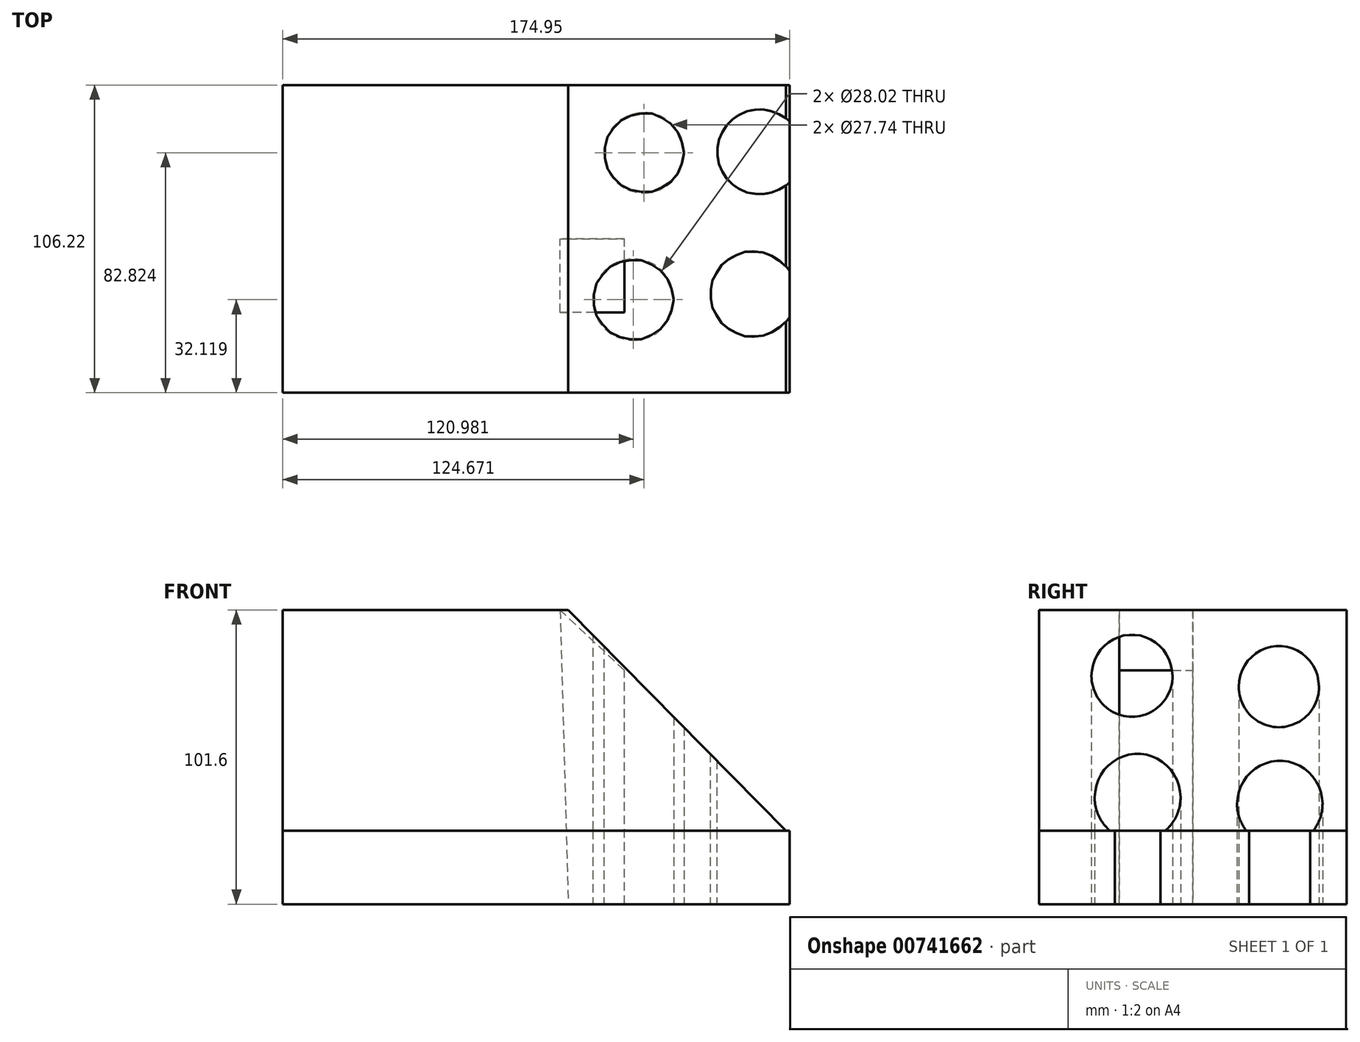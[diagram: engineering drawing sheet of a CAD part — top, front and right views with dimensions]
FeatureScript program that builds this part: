
annotation { "Feature Type Name" : "Feature", "Feature Type Description" : "" }
export const myFeature = defineFeature(function(context is Context, id is Id, definition is map)
    precondition{}
    {
        {
            var Q0;
            Q0=qCreatedBy(makeId("Top.planeOp"),FACE);
            var sketch = newSketch(context, id + "F0", { "sketchPlane" : qUnion([Q0])});
            skLineSegment(sketch, "E0.bottom", {"start": v(98.54, 53.1) * mm, "end": v(-98.54, 53.1) * mm});
            skLineSegment(sketch, "E0.top", {"start": v(98.54, -53.1) * mm, "end": v(-98.54, -53.1) * mm});
            skLineSegment(sketch, "E0.left", {"start": v(98.54, 53.1) * mm, "end": v(98.54, -53.1) * mm});
            skLineSegment(sketch, "E0.right", {"start": v(-98.54, 53.1) * mm, "end": v(-98.54, -53.1) * mm});
            skPoint(sketch, "E0.middle", {"position": v(0, 0) * mm});
            skSolve(sketch);
        }
        {
            var Q0;
            Q0=makeQuery(id+"F0.imprint","IMPRINT",FACE,{"disambiguationData":[TD([[makeQuery(id+"F0.imprint","IMPRINT",EDGE,{"derivedFrom":sQuery(id+"F0.wireOp",EDGE,"E0.bottom")}),1.0]])]});
            var sketch = newSketch(context, id + "F1", { "sketchPlane" : qUnion([Q0])});
            skCircle(sketch, "E1", {"center": v(26.13, 29.71) * mm, "radius": 13.87 * mm});
            skCircle(sketch, "E2", {"center": v(66.09, 30.03) * mm, "radius": 14.75 * mm});
            skCircle(sketch, "E3", {"center": v(22.44, -21) * mm, "radius": 14.01 * mm});
            skCircle(sketch, "E4", {"center": v(63.84, -19.07) * mm, "radius": 14.85 * mm});
            skSolve(sketch);
        }
        {
            var Q0;
            Q0=makeQuery(id+"F1.imprint","IMPRINT",FACE,{"disambiguationData":[TD([[makeQuery(id+"F1.imprint","IMPRINT",EDGE,{"derivedFrom":sQuery(id+"F1.wireOp",EDGE,"E1")}),-1.0]])]});
            var sketch = newSketch(context, id + "F2", { "sketchPlane" : qUnion([Q0])});
            skLineSegment(sketch, "E5.bottom", {"start": v(98.57, -53.13) * mm, "end": v(76.41, -53.13) * mm});
            skLineSegment(sketch, "E5.top", {"start": v(98.57, -43.68) * mm, "end": v(76.41, -43.68) * mm});
            skLineSegment(sketch, "E5.left", {"start": v(98.57, -53.13) * mm, "end": v(98.57, -43.68) * mm});
            skLineSegment(sketch, "E5.right", {"start": v(76.41, -53.13) * mm, "end": v(76.41, -43.68) * mm});
            skSolve(sketch);
        }
        {
            var Q0;
            Q0=makeQuery(id+"F2.imprint","IMPRINT",FACE,{"disambiguationData":[TD([[makeQuery(id+"F2.imprint","IMPRINT",EDGE,{"derivedFrom":makeQuery(id+"F1.imprint","IMPRINT",EDGE,{"derivedFrom":sQuery(id+"F1.wireOp",EDGE,"E1")})}),-1.0]])]});
            var Q1;
            Q1 = qSketchRegion(id + "F0", true);
            extrude(context, id + "F3", {"entities" : qUnion([Q0, Q1]), "depth" : 25.4 * mm, "offsetDistance" : 25.4 * mm});
        }
        {
            var Q0;
            Q0 = qSketchRegion(id + "F2", true);
            extrude(context, id + "F4", {"entities" : qUnion([Q0]), "operationType" : NewBodyOperationType.REMOVE, "oppositeDirection" : true, "depth" : 25.4 * mm, "offsetDistance" : 25.4 * mm});
        }
        {
            var Q0;
            Q0 = qSketchRegion(id + "F2", true);
            extrude(context, id + "F5", {"entities" : qUnion([Q0]), "operationType" : NewBodyOperationType.REMOVE, "depth" : 25.4 * mm, "offsetDistance" : 25.4 * mm});
        }
        {
            var Q0;
            Q0=makeQuery(id+"F3.opExtrude","CAP_FACE",FACE,{"disambiguationData":[OSD([sQuery(id+"F0.wireOp",EDGE,"E0.bottom"),sQuery(id+"F0.wireOp",EDGE,"E0.top"),sQuery(id+"F0.wireOp",EDGE,"E0.left"),sQuery(id+"F0.wireOp",EDGE,"E0.right"),sQuery(id+"F1.wireOp",EDGE,"E1"),sQuery(id+"F1.wireOp",EDGE,"E2"),sQuery(id+"F1.wireOp",EDGE,"E3"),sQuery(id+"F1.wireOp",EDGE,"E4"),sQuery(id+"F2.wireOp",EDGE,"E5.top"),sQuery(id+"F2.wireOp",EDGE,"E5.right")])],"isStart":false});
            extrude(context, id + "F6", {"entities" : qUnion([Q0]), "depth" : 76.2 * mm, "offsetDistance" : 25.4 * mm});
        }
        {
            var Q0;
            Q0=makeQuery(id+"F6.opExtrude","SWEPT_FACE",FACE,{"disambiguationData":[OSD([sQuery(id+"F0.wireOp",EDGE,"E0.top")])]});
            var sketch = newSketch(context, id + "F7", { "sketchPlane" : qUnion([Q0])});
            skLineSegment(sketch, "E6", {"start": v(100.27, 0) * mm, "end": v(0, 101.6) * mm});
            skLineSegment(sketch, "E7", {"start": v(98.03, 101.6) * mm, "end": v(100.27, 0) * mm});
            skSolve(sketch);
        }
        {
            var Q0;
            Q0=makeQuery(id+"F6.opExtrude","SWEPT_FACE",FACE,{"disambiguationData":[OSD([sQuery(id+"F2.wireOp",EDGE,"E5.top")])]});
            extrude(context, id + "F8", {"entities" : qUnion([Q0]), "operationType" : NewBodyOperationType.REMOVE, "oppositeDirection" : true, "depth" : 127 * mm, "offsetDistance" : 25.4 * mm});
        }
        {
            var Q0;
            {var subQ1=sQuery(id+"F0.wireOp",EDGE,"E0.top");var subQ6=makeQuery(id+"F6.opExtrude","SWEPT_EDGE",EDGE,{"disambiguationData":[OSD([subQ1,sQuery(id+"F2.wireOp",EDGE,"E5.right")])]});Q0=makeQuery(id+"F7.imprint","IMPRINT",FACE,{"disambiguationData":[TD([[makeQuery(id+"F7.imprint","IMPRINT",EDGE,{"derivedFrom":subQ6}),-1.0]])]});}
            extrude(context, id + "F9", {"entities" : qUnion([Q0]), "operationType" : NewBodyOperationType.REMOVE, "oppositeDirection" : true, "depth" : 127 * mm, "offsetDistance" : 25.4 * mm});
        }
        {
            var Q0;
            Q0=makeQuery(id+"F5.boolean.opBoolean","COPY",FACE,{"derivedFrom":makeQuery(id+"F5.opExtrude","SWEPT_FACE",FACE,{"disambiguationData":[OSD([sQuery(id+"F2.wireOp",EDGE,"E5.top")])]})});
            var sketch = newSketch(context, id + "F10", { "sketchPlane" : qUnion([Q0])});
            skLineSegment(sketch, "E8", {"start": v(76.41, 25.4) * mm, "end": v(98.54, 0) * mm});
            skLineSegment(sketch, "E9", {"start": v(98.54, 0) * mm, "end": v(76.41, 0) * mm});
            skLineSegment(sketch, "E10", {"start": v(76.41, 0) * mm, "end": v(76.41, 25.4) * mm});
            skSolve(sketch);
        }
        {
            var Q0;
            Q0=makeQuery(id+"F10.imprint","IMPRINT",FACE,{"disambiguationData":[TD([[makeQuery(id+"F10.imprint","IMPRINT",EDGE,{"derivedFrom":sQuery(id+"F10.wireOp",EDGE,"E8")}),-1.0]])]});
            extrude(context, id + "F11", {"entities" : qUnion([Q0]), "operationType" : NewBodyOperationType.REMOVE, "oppositeDirection" : true, "depth" : 127 * mm, "offsetDistance" : 25.4 * mm});
        }
        {
            var Q0;
            Q0=makeQuery(id+"F10.imprint","IMPRINT",FACE,{"disambiguationData":[TD([[makeQuery(id+"F10.imprint","IMPRINT",EDGE,{"derivedFrom":sQuery(id+"F10.wireOp",EDGE,"E8")}),1.0]])]});
            extrude(context, id + "F12", {"entities" : qUnion([Q0]), "operationType" : NewBodyOperationType.REMOVE, "oppositeDirection" : true, "depth" : 127 * mm, "offsetDistance" : 25.4 * mm});
        }
        {
            var Q0;
            Q0=qCreatedBy(makeId("Front.planeOp"),FACE);
            var sketch = newSketch(context, id + "F13", { "sketchPlane" : qUnion([Q0])});
            skLineSegment(sketch, "E11", {"start": v(19.34, 0) * mm, "end": v(19.34, 80.72) * mm});
            skLineSegment(sketch, "E12", {"start": v(19.34, 80.72) * mm, "end": v(-2.78, 101.51) * mm});
            skLineSegment(sketch, "E13", {"start": v(-2.78, 101.51) * mm, "end": v(0, 0) * mm});
            skLineSegment(sketch, "E14", {"start": v(0, 0) * mm, "end": v(19.34, 0) * mm});
            skSolve(sketch);
        }
        {
            var Q0;
            Q0 = qSketchRegion(id + "F13", true);
            extrude(context, id + "F14", {"entities" : qUnion([Q0]), "depth" : 25.4 * mm, "offsetDistance" : 25.4 * mm});
        }
    });
